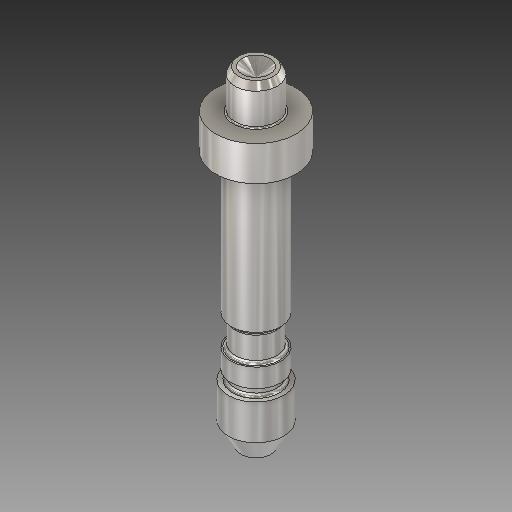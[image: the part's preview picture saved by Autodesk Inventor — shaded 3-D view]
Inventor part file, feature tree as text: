
AUTODESK INVENTOR PART (.ipt)
format: ipt  version: 2019 (Build 230136000, 136)  size: 183,808 bytes
history: native  units: in
note: dims shown in document units (in); Inventor stores cm internally (conversion verified against a paired STEP export)
features: other x3, sketch x1
ambient origin geometry x8: Origin, YZ Plane, XZ Plane, XY Plane, X Axis, Y Axis, Z Axis, Center Point
bodies: Solid1 (feature_tree)
feature tree (4):
  other  "Side Handle Pivot Pin.ipt"
  other  "Solid1::Side Handle Pivot Pin.ipt"
  other  "TaggingFeature1"
  sketch  "Sketch1"  dims[d0=0.3937in]
